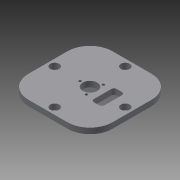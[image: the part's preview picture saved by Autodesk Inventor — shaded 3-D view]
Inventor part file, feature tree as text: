
AUTODESK INVENTOR PART (.ipt)
format: ipt  version: 2015 (Build 190159000, 159)  size: 139,264 bytes
history: native  units: in
note: dims shown in document units (in); Inventor stores cm internally (conversion verified against a paired STEP export)
features: extrude x2, fillet x2, sketch x2
ambient origin geometry x8: Origin, YZ Plane, XZ Plane, XY Plane, X Axis, Y Axis, Z Axis, Center Point
bodies: Body1 (feature_tree)
feature tree (6):
  extrude  "Extrusion6"  TaperAngle=120.0deg  [1 undecoded]
  fillet  "Fillet1"  Radius=0.4375in
  extrude  "Extrusion7"  Depth=0.4375in
  fillet  "Fillet2"  Radius=0.1174in
  sketch  "Sketch3"  dims[d19=120.0deg d20=120.0deg d21=0.4375in]
  sketch  "Sketch4"  dims[d22=0.4375in d23=0.4375in d24=0.1174in d25=0.1174in d26=0.1174in d27=3.1496in d28=3.1496in d29=0.3976in d30=0.3976in d31=3.75in d32=3.75in d33=0.25in d34=0.0in d35=1.0in d36=0.65in d39=0.476in d40=1.024in d41=0.8in d42=1.0in d43=0.0in d44=0.125in]
note: 1 required parameter value undecoded (feature->parameter linkage not recoverable at this tier; creation-order binding heuristic only, values carry confidence <= 0.55)
